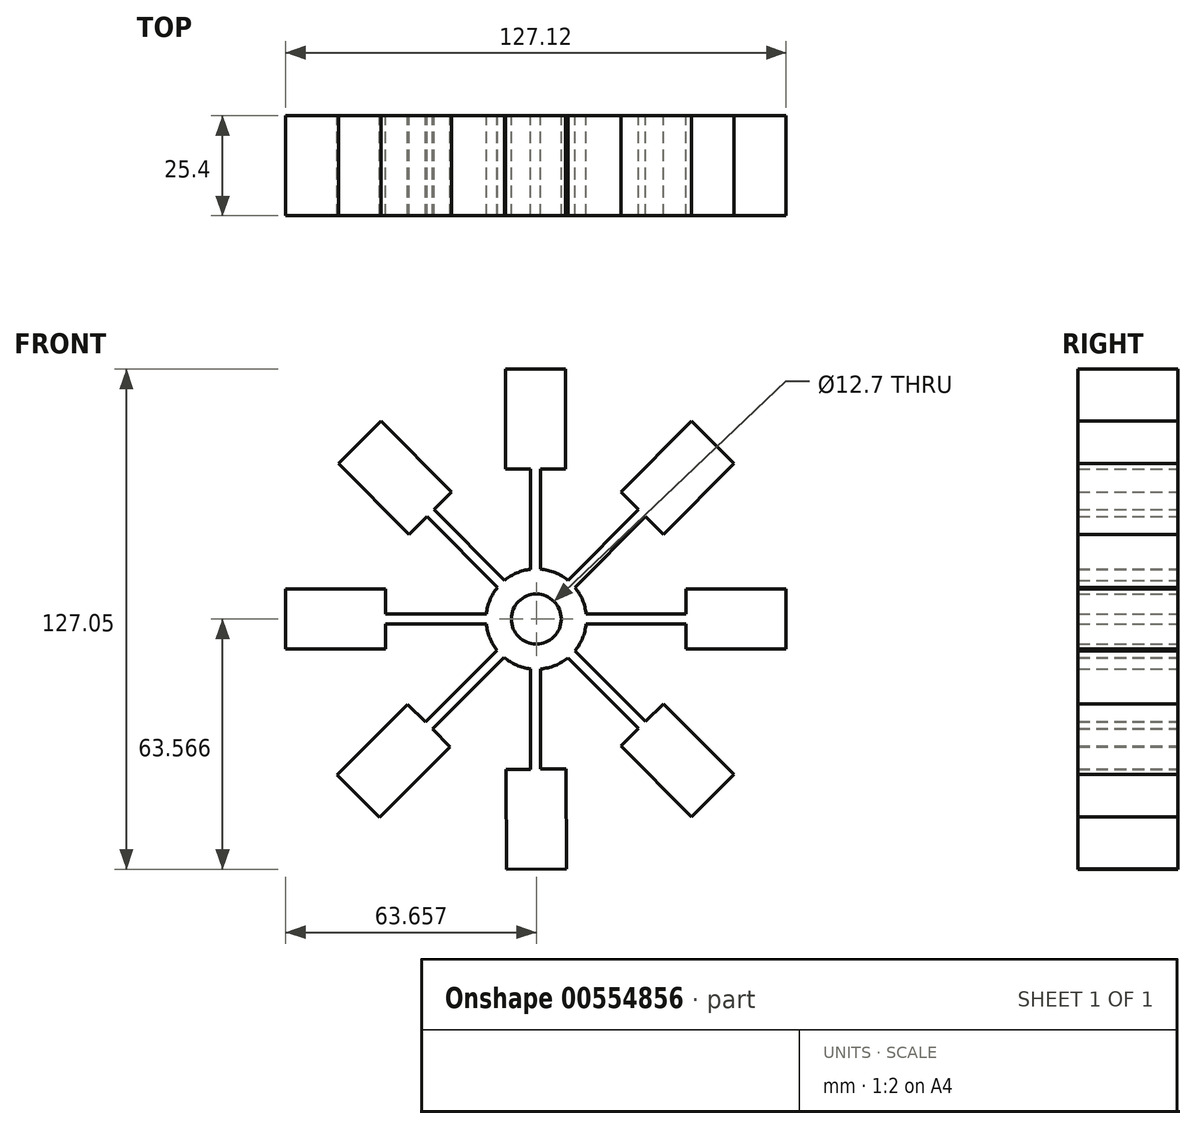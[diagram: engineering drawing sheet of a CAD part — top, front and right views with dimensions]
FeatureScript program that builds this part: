
annotation { "Feature Type Name" : "Feature", "Feature Type Description" : "" }
export const myFeature = defineFeature(function(context is Context, id is Id, definition is map)
    precondition{}
    {
        {
            var Q0;
            Q0=qCreatedBy(makeId("Front.planeOp"),FACE);
            var sketch = newSketch(context, id + "F0", { "sketchPlane" : qUnion([Q0])});
            skCircle(sketch, "E0", {"center": v(-7.41, 46.1) * mm, "radius": 12.72 * mm});
            skLineSegment(sketch, "E1", {"start": v(-6.35, 58.79) * mm, "end": v(-6.35, 84.19) * mm});
            skLineSegment(sketch, "E2", {"start": v(-20.07, 47.38) * mm, "end": v(-45.67, 47.38) * mm});
            skLineSegment(sketch, "E3", {"start": v(-20.07, 44.84) * mm, "end": v(-45.67, 44.84) * mm});
            skLineSegment(sketch, "E4", {"start": v(-17.35, 38.16) * mm, "end": v(-35.5, 20) * mm});
            skLineSegment(sketch, "E5", {"start": v(-15.57, 36.34) * mm, "end": v(-33.77, 18.14) * mm});
            skLineSegment(sketch, "E6", {"start": v(-17.26, 54.16) * mm, "end": v(-35.22, 72.12) * mm});
            skLineSegment(sketch, "E7", {"start": v(-15.47, 55.96) * mm, "end": v(-33.43, 73.92) * mm});
            skLineSegment(sketch, "E8", {"start": v(2.44, 38.05) * mm, "end": v(20.4, 20.1) * mm});
            skLineSegment(sketch, "E9", {"start": v(0.64, 36.26) * mm, "end": v(18.6, 18.3) * mm});
            skLineSegment(sketch, "E10", {"start": v(18.6, 18.3) * mm, "end": v(20.4, 20.1) * mm});
            skLineSegment(sketch, "E11", {"start": v(-35.5, 20) * mm, "end": v(-33.77, 18.14) * mm});
            skLineSegment(sketch, "E12", {"start": v(-45.67, 44.84) * mm, "end": v(-45.67, 47.38) * mm});
            skLineSegment(sketch, "E13", {"start": v(-33.43, 73.92) * mm, "end": v(-35.22, 72.12) * mm});
            skCircle(sketch, "E14", {"center": v(-7.41, 46.1) * mm, "radius": 6.35 * mm});
            skLineSegment(sketch, "E15", {"start": v(-15.24, 84.19) * mm, "end": v(0, 84.19) * mm});
            skLineSegment(sketch, "E16", {"start": v(0, 84.19) * mm, "end": v(0, 109.59) * mm});
            skLineSegment(sketch, "E17", {"start": v(0, 109.59) * mm, "end": v(-15.24, 109.59) * mm});
            skLineSegment(sketch, "E18", {"start": v(-15.24, 109.59) * mm, "end": v(-15.24, 84.19) * mm});
            skLineSegment(sketch, "E19", {"start": v(-28.94, 78.4) * mm, "end": v(-46.9, 96.37) * mm});
            skLineSegment(sketch, "E20", {"start": v(-39.71, 67.63) * mm, "end": v(-57.68, 85.6) * mm});
            skLineSegment(sketch, "E21", {"start": v(-57.68, 85.6) * mm, "end": v(-46.9, 96.37) * mm});
            skLineSegment(sketch, "E22", {"start": v(-35.22, 72.12) * mm, "end": v(-39.71, 67.63) * mm});
            skLineSegment(sketch, "E23", {"start": v(-33.43, 73.92) * mm, "end": v(-28.94, 78.4) * mm});
            skLineSegment(sketch, "E24", {"start": v(-45.67, 44.84) * mm, "end": v(-45.67, 38.49) * mm});
            skLineSegment(sketch, "E25", {"start": v(-45.67, 38.49) * mm, "end": v(-71.07, 38.49) * mm});
            skLineSegment(sketch, "E26", {"start": v(-71.07, 38.49) * mm, "end": v(-71.07, 53.73) * mm});
            skLineSegment(sketch, "E27", {"start": v(-71.07, 53.73) * mm, "end": v(-45.67, 53.73) * mm});
            skLineSegment(sketch, "E28", {"start": v(-45.67, 53.73) * mm, "end": v(-45.67, 47.38) * mm});
            skLineSegment(sketch, "E29", {"start": v(-33.77, 18.14) * mm, "end": v(-29.28, 13.65) * mm});
            skLineSegment(sketch, "E30", {"start": v(-29.28, 13.65) * mm, "end": v(-47.24, -4.3) * mm});
            skLineSegment(sketch, "E31", {"start": v(-47.24, -4.3) * mm, "end": v(-58.01, 6.47) * mm});
            skLineSegment(sketch, "E32", {"start": v(-58.01, 6.47) * mm, "end": v(-40.05, 24.43) * mm});
            skLineSegment(sketch, "E33", {"start": v(-40.05, 24.43) * mm, "end": v(-35.5, 20) * mm});
            skLineSegment(sketch, "E34", {"start": v(5.25, 44.84) * mm, "end": v(30.65, 44.84) * mm});
            skLineSegment(sketch, "E35", {"start": v(5.25, 47.38) * mm, "end": v(30.65, 47.38) * mm});
            skLineSegment(sketch, "E36", {"start": v(30.65, 47.38) * mm, "end": v(30.65, 44.84) * mm});
            skLineSegment(sketch, "E37", {"start": v(2.44, 54.16) * mm, "end": v(20.4, 72.12) * mm});
            skLineSegment(sketch, "E38", {"start": v(0.64, 55.96) * mm, "end": v(18.6, 73.92) * mm});
            skLineSegment(sketch, "E39", {"start": v(18.6, 73.92) * mm, "end": v(20.4, 72.12) * mm});
            skLineSegment(sketch, "E40.MirrorCS", {"start": v(-15.1, 7.94) * mm, "end": v(0.15, 8) * mm});
            skLineSegment(sketch, "E41.MirrorCS", {"start": v(-14.99, -17.46) * mm, "end": v(-15.1, 7.94) * mm});
            skLineSegment(sketch, "E42.MirrorCS", {"start": v(0.25, -17.4) * mm, "end": v(-14.99, -17.46) * mm});
            skLineSegment(sketch, "E43.MirrorCS", {"start": v(0.15, 8) * mm, "end": v(0.25, -17.4) * mm});
            skLineSegment(sketch, "E44", {"start": v(20.4, 20.1) * mm, "end": v(24.89, 24.58) * mm});
            skLineSegment(sketch, "E45", {"start": v(24.89, 24.58) * mm, "end": v(42.85, 6.62) * mm});
            skLineSegment(sketch, "E46", {"start": v(42.85, 6.62) * mm, "end": v(32.07, -4.16) * mm});
            skLineSegment(sketch, "E47", {"start": v(32.07, -4.16) * mm, "end": v(14.11, 13.8) * mm});
            skLineSegment(sketch, "E48", {"start": v(14.11, 13.8) * mm, "end": v(18.6, 18.3) * mm});
            skLineSegment(sketch, "E49", {"start": v(30.65, 44.84) * mm, "end": v(30.65, 38.49) * mm});
            skLineSegment(sketch, "E50", {"start": v(30.65, 38.49) * mm, "end": v(56.05, 38.49) * mm});
            skLineSegment(sketch, "E51", {"start": v(56.05, 38.49) * mm, "end": v(56.05, 53.73) * mm});
            skLineSegment(sketch, "E52", {"start": v(56.05, 53.73) * mm, "end": v(30.65, 53.73) * mm});
            skLineSegment(sketch, "E53", {"start": v(30.65, 53.73) * mm, "end": v(30.65, 47.38) * mm});
            skLineSegment(sketch, "E54", {"start": v(18.6, 73.92) * mm, "end": v(14.11, 78.4) * mm});
            skLineSegment(sketch, "E55", {"start": v(20.4, 72.12) * mm, "end": v(24.89, 67.63) * mm});
            skLineSegment(sketch, "E56", {"start": v(24.89, 67.63) * mm, "end": v(42.85, 85.6) * mm});
            skLineSegment(sketch, "E57", {"start": v(42.85, 85.6) * mm, "end": v(32.07, 96.37) * mm});
            skLineSegment(sketch, "E58", {"start": v(32.07, 96.37) * mm, "end": v(14.11, 78.4) * mm});
            skLineSegment(sketch, "E59", {"start": v(-8.89, 58.74) * mm, "end": v(-8.89, 84.19) * mm});
            skLineSegment(sketch, "E60", {"start": v(-6.35, 33.43) * mm, "end": v(-6.35, 7.97) * mm});
            skLineSegment(sketch, "E61", {"start": v(-8.89, 33.47) * mm, "end": v(-8.89, 7.96) * mm});
            skSolve(sketch);
        }
        {
            var Q0;
            Q0 = qSketchRegion(id + "F0", true);
            extrude(context, id + "F1", {"entities" : qUnion([Q0]), "depth" : 25.4 * mm, "offsetDistance" : 25.4 * mm});
        }
    });
